# Revit family: AFX-Sienna-LED_Vanity
name_source: partatom
category: Lighting Fixtures
units: mm (PartAtom-declared; Revit-internal decimal feet)

## family parameters
Cut with Voids When Loaded = No
Host = Face
Light Source = Yes
Part Type = Normal
Room Calculation Point = No
Round Connector Dimension = Use Diameter
Shared = No

## types (2) — shared parameters
Apparent Load = 0 VA
Assembly Code = D5020200
Canopy Finish = AFX - Black Steel
Color Filter = 16777215
Colour Rendering Index = 90
Default Elevation = 48"
Depth = 1 31/32"
Diffuser Finish = AFX - White Acrylic
Dimming Lamp Color Temperature Shift = <None>
Emit Shape Visible in Rendering = No
Emit from Rectangle Length = 48"
Emit from Rectangle Width = 24"
Frame Finish = AFX - Black Steel
Height = 4 3/4"
Keynote = 12500
Lamp = LED
Manufacturer = AFX Inc
Power Factor = 1
Product Documentation Link = https://www.afxinc.com
Tilt Angle = -90.00°
Type Comments = Sienna
URL = https://www.afxinc.com
Voltage = 120 V

## per-type parameters (varying)
| type | Description | Length | Photometric Web File | Wattage Comments |
| SIEV3405LAJD1BK | LED Vanity - 34 1/2"L x 2"D x 4 3/4"H | 34 1/2" | SIEV3405LAJD1XX LR37496-W1L.IES | 26 |
| SIEV2305LAJD1BK | LED Vanity - 22 3/4"L x 2"D x 4 3/4"H | 22 3/4" | SIEV2305LAJD1XX LR37496-W1M.IES | 19 |

note: column(s) folded — value = type name in every type: Model

## geometry (parser evidence)
native form markers: Sweep x2
no freeform markers — native parametric forms only
